# Revit family: Atlas_Sound_DR-54
name_source: partatom
category: Communication Devices
units: mm (PartAtom-declared; Revit-internal decimal feet)

## family parameters
Always vertical = No
Cut with Voids When Loaded = No
Maintain Annotation Orientation = No
Part Type = Normal
Room Calculation Point = No
Round Connector Dimension = Use Diameter
Shared = No
Work Plane-Based = Yes

## types (1)
- Horn Loudspeaker
    100V Taps = 32.00 W
    70V Taps = 32.00 W
    Baffle Material = <By Category>
    Body Material = QF_Plastic - Black - Fine Textured
    Color = <By Category>
    Cost = 215.99 $
    Cost MSRP = 215.99 $
    Coverage Horizontal = 75.00°
    Coverage Vertical = 0.00°
    Default Elevation = 48 "
    Depth = 19.19 "
    Description = 75° UNIFORM COVERAGE HORN
    Dispersion Angle = 75.00°
    Enclosure Material = <By Category>
    Family Code (default) = LOUD SPEAKERS
    Grill Material = <By Category>
    Height = 22.17 "
    IQ Category = SPEAKERS
    Ingress Protection = IP-34
    Manufacturer = ATLAS SOUND
    Manufacturer URL = https://www.atlasied.com
    Market = Commercial, Higher Education, Emergency
    MasterFormat = 27 41 13
    MaterFormat Title = SPEAKERS
    Max Input Ratings (8Ω) = TBD
    Model = DR-54
    Mount Material = QF_Plastic - Black - Fine Textured
    OmniClass Number = 23-37 17 13 19
    OmniClass Title = SPEAKERS
    Pitch = 0.00°
    Product Documentation Link = https://www.atlasied.com
    Product Page URL = https://www.atlasied.com
    Rotation = 0.00°
    SPL Max = 125
    ScheduleType |RF| = AtlasIED Master
    Transformer Option = Yes
    URL = www.atlassound.com
    Vertical Symmetry = Yes
    Warranty = 5 Year
    Weight Product = 20
    Width = 25.22 "

## geometry (parser evidence)
native form markers: Blend x10, Sweep x4
no freeform markers — native parametric forms only
